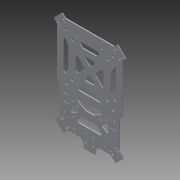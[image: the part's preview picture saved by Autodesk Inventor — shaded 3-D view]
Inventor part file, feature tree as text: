
AUTODESK INVENTOR PART (.ipt)
format: ipt  version: 2013 (Build 170138000, 138)  size: 6,375,936 bytes
history: native  units: mm
features: sketch x9, hole x5, extrude x4, other x2, fillet x1
ambient origin geometry x8: Origin, YZ Plane, XZ Plane, XY Plane, X Axis, Y Axis, Z Axis, Center Point
feature tree (21):
  other  "ソリッド1"
  extrude  "押し出し1"  Depth=115.0mm
  hole  "穴1"  [1 undecoded]
  hole  "穴2"  [1 undecoded]
  hole  "穴6"  [1 undecoded]
  hole  "穴7"  [1 undecoded]
  hole  "穴8"  [1 undecoded]
  extrude  "押し出し7"  TaperAngle=0.0deg  [1 undecoded]
  extrude  "押し出し8"  Depth=2.0mm TaperAngle=0.0deg
  extrude  "押し出し12"  Depth=3.2mm
  fillet  "フィレット1"  Radius=30.0mm
  sketch  "スケッチ1"
  sketch  "スケッチ2"
  sketch  "スケッチ3"
  sketch  "スケッチ9"
  sketch  "スケッチ11"
  sketch  "スケッチ12"
  sketch  "スケッチ13"
  sketch  "スケッチ14"
  sketch  "スケッチ17"
  other  "断面エッジを投影1"
note: 6 required parameter values undecoded (feature->parameter linkage not recoverable at this tier; creation-order binding heuristic only, values carry confidence <= 0.55)
